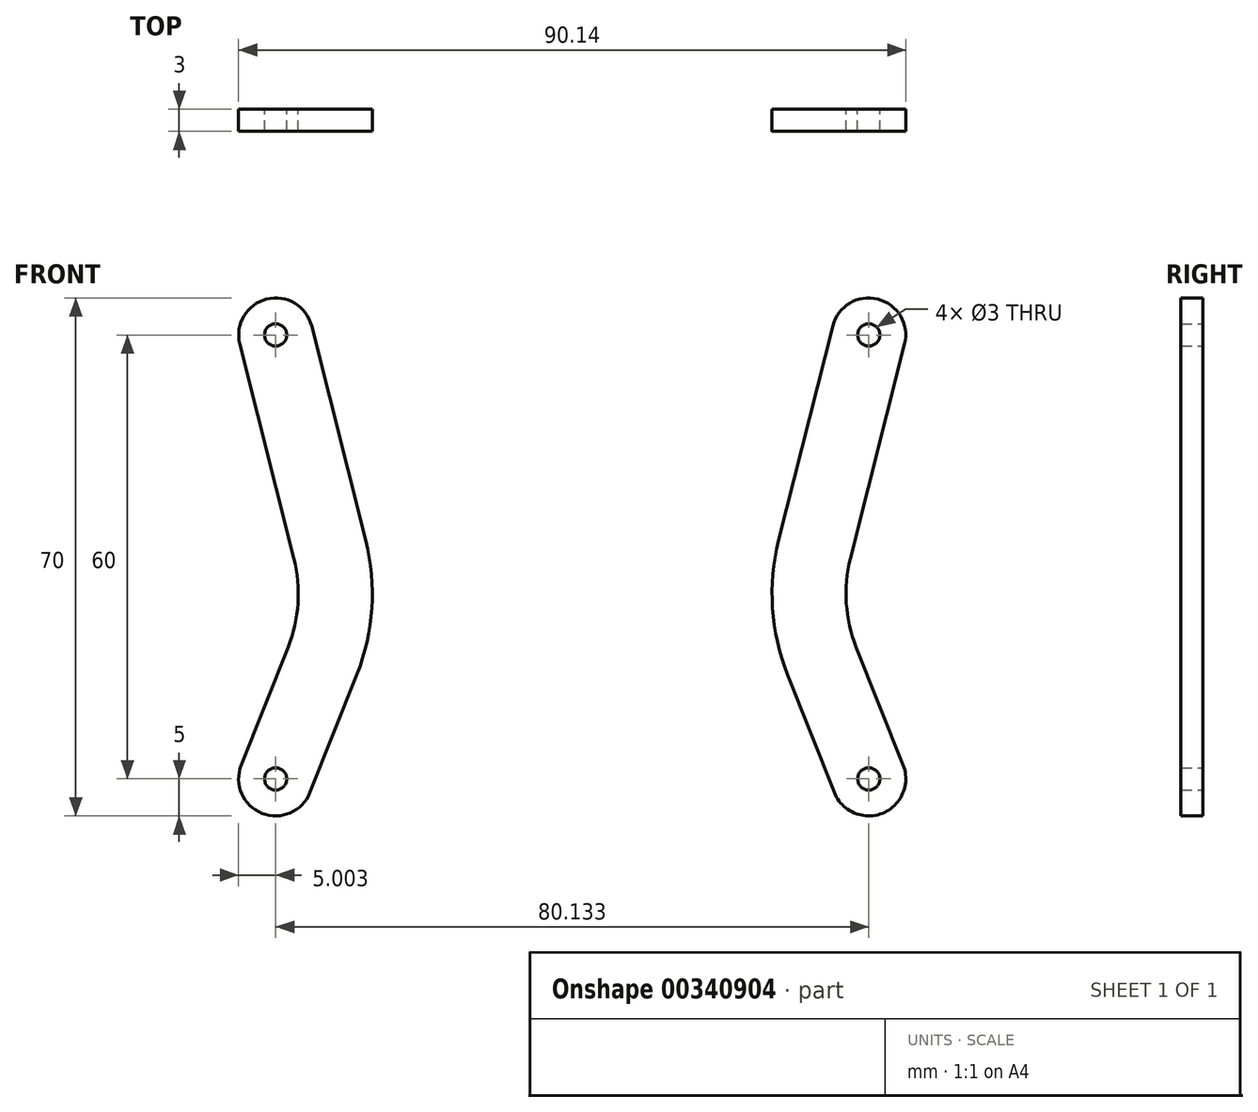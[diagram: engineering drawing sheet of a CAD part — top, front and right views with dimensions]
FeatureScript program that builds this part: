
annotation { "Feature Type Name" : "Feature", "Feature Type Description" : "" }
export const myFeature = defineFeature(function(context is Context, id is Id, definition is map)
    precondition{}
    {
        {
            var Q0;
            Q0=qCreatedBy(makeId("Front.planeOp"),FACE);
            var sketch = newSketch(context, id + "F0", { "sketchPlane" : qUnion([Q0])});
            skLineSegment(sketch, "E0", {"start": v(8.07, -25) * mm, "end": v(1.72, -9.02) * mm});
            skLineSegment(sketch, "E1", {"start": v(0.74, 5.98) * mm, "end": v(8.07, 35) * mm});
            skArc(sketch, "E2", {"start": v(0.74, 5.98) * mm, "mid": v(0.05, -1.6) * mm, "end": v(1.72, -9.02) * mm});
            skArc(sketch, "E3.0.left", {"start": v(5.6, 4.76) * mm, "mid": v(5.04, -1.27) * mm, "end": v(6.37, -7.17) * mm});
            skArc(sketch, "E3.0.right", {"start": v(-4.1, 7.2) * mm, "mid": v(-4.94, -1.92) * mm, "end": v(-2.92, -10.86) * mm});
            skArc(sketch, "E3.1.startCap", {"start": v(12.71, -23.16) * mm, "mid": v(9.91, -29.65) * mm, "end": v(3.42, -26.84) * mm});
            skLineSegment(sketch, "E3.1.left", {"start": v(3.42, -26.84) * mm, "end": v(-2.92, -10.86) * mm});
            skLineSegment(sketch, "E3.1.right", {"start": v(12.71, -23.16) * mm, "end": v(6.37, -7.17) * mm});
            skArc(sketch, "E3.2.endCap", {"start": v(3.22, 36.22) * mm, "mid": v(9.3, 39.85) * mm, "end": v(12.91, 33.78) * mm});
            skLineSegment(sketch, "E3.2.left", {"start": v(-4.1, 7.2) * mm, "end": v(3.22, 36.22) * mm});
            skLineSegment(sketch, "E3.2.right", {"start": v(5.6, 4.76) * mm, "end": v(12.91, 33.78) * mm});
            skPoint(sketch, "E4", {"position": v(0, 0) * mm});
            skSolve(sketch);
        }
        {
            var Q0;
            Q0 = qSketchRegion(id + "F0", true);
            extrude(context, id + "F1", {"entities" : qUnion([Q0]), "depth" : 3 * mm, "offsetDistance" : 25 * mm});
        }
        {
            var Q0;
            Q0=sQuery(id+"F0.wireOp",VERTEX,"E1.end");
            var Q1;
            Q1=sQuery(id+"F0.wireOp",VERTEX,"E0.start");
            var Q2;
            Q2=makeQuery(id+"F1.opExtrude","SWEPT_BODY",BODY,{"disambiguationData":[OSD([sQuery(id+"F0.wireOp",EDGE,"E3.0.left"),sQuery(id+"F0.wireOp",EDGE,"E3.0.right"),sQuery(id+"F0.wireOp",EDGE,"E3.1.startCap"),sQuery(id+"F0.wireOp",EDGE,"E3.1.left"),sQuery(id+"F0.wireOp",EDGE,"E3.1.right"),sQuery(id+"F0.wireOp",EDGE,"E3.2.endCap"),sQuery(id+"F0.wireOp",EDGE,"E3.2.left"),sQuery(id+"F0.wireOp",EDGE,"E3.2.right")])]});
            hole(context, id + "F2", {"style" : HoleStyle.SIMPLE, "endStyle" : HoleEndStyle.THROUGH, "oppositeDirection" : true, "holeDiameter" : 3 * mm, "majorDiameter" : 5 * mm, "isTappedThrough" : true, "tappedDepth" : 12 * mm, "tapClearance" : 3, "locations" : qUnion([Q0, Q1]), "scope" : qUnion([Q2])});
        }
        {
            var Q0;
            Q0=qCreatedBy(makeId("Right.planeOp"),FACE);
            cPlane(context, id + "F3", {"entities" : qUnion([Q0]), "cplaneType" : CPlaneType.OFFSET, "offset" : 32 * mm, "oppositeDirection" : true, "width" : 150 * mm, "height" : 150 * mm});
        }
        {
            var Q0;
            Q0=makeQuery(id+"F1.opExtrude","SWEPT_BODY",BODY,{"disambiguationData":[OSD([sQuery(id+"F0.wireOp",EDGE,"E3.0.left"),sQuery(id+"F0.wireOp",EDGE,"E3.0.right"),sQuery(id+"F0.wireOp",EDGE,"E3.1.startCap"),sQuery(id+"F0.wireOp",EDGE,"E3.1.left"),sQuery(id+"F0.wireOp",EDGE,"E3.1.right"),sQuery(id+"F0.wireOp",EDGE,"E3.2.endCap"),sQuery(id+"F0.wireOp",EDGE,"E3.2.left"),sQuery(id+"F0.wireOp",EDGE,"E3.2.right")])]});
            var Q1;
            Q1=qCreatedBy(id+"F3.planeOp",FACE);
            mirror(context, id + "F4", {"entities" : qUnion([Q0]), "mirrorPlane" : qUnion([Q1])});
        }
    });
